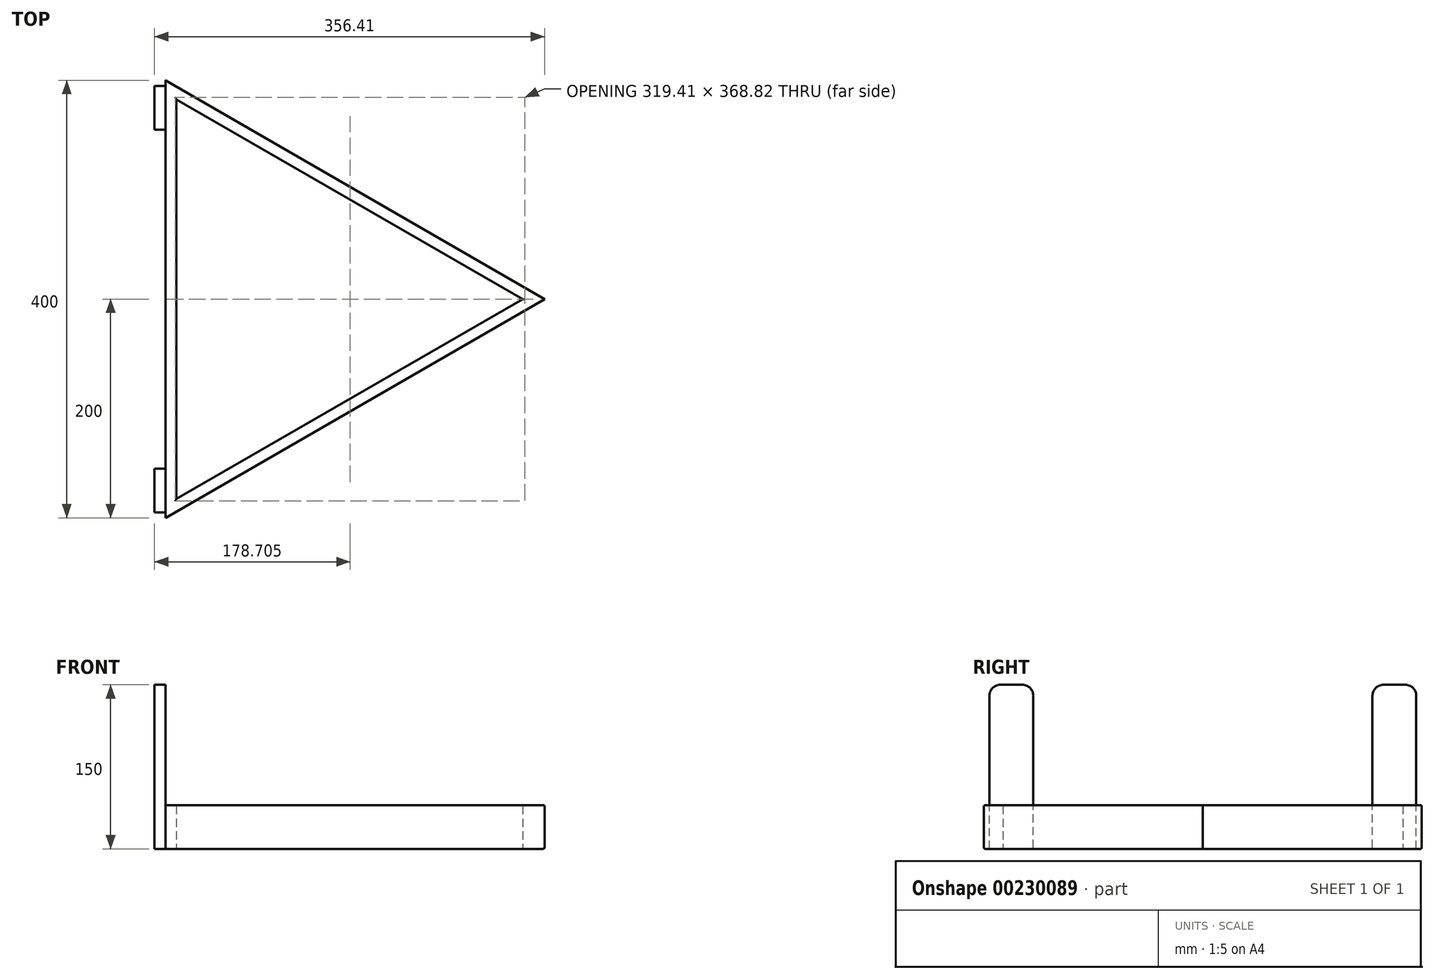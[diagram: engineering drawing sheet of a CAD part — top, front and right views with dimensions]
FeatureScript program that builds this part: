
annotation { "Feature Type Name" : "Feature", "Feature Type Description" : "" }
export const myFeature = defineFeature(function(context is Context, id is Id, definition is map)
    precondition{}
    {
        {
            var Q0;
            Q0=qCreatedBy(makeId("Top.planeOp"),FACE);
            var sketch = newSketch(context, id + "F0", { "sketchPlane" : qUnion([Q0])});
            skLineSegment(sketch, "E0", {"start": v(0, 0) * mm, "end": v(-346.41, 200) * mm});
            skLineSegment(sketch, "E1", {"start": v(-346.41, 200) * mm, "end": v(-346.41, -200) * mm});
            skLineSegment(sketch, "E2", {"start": v(-346.41, -200) * mm, "end": v(0, 0) * mm});
            skLineSegment(sketch, "E3", {"start": v(-20, 0) * mm, "end": v(-336.41, 182.68) * mm});
            skLineSegment(sketch, "E4", {"start": v(-336.41, 182.68) * mm, "end": v(-336.41, -182.68) * mm});
            skLineSegment(sketch, "E5", {"start": v(-336.41, -182.68) * mm, "end": v(-20, 0) * mm});
            skSolve(sketch);
        }
        {
            var Q0;
            Q0=qSketchRegion(id+"F0",true);
            extrude(context, id + "F1", {"entities" : qUnion([Q0]), "depth" : 40 * mm});
        }
        {
            var Q0;
            Q0=makeQuery(id+"F1.opExtrude","SWEPT_FACE",FACE,{"disambiguationData":[OSD([sQuery(id+"F0.wireOp",EDGE,"E1")])]});
            var sketch = newSketch(context, id + "F2", { "sketchPlane" : qUnion([Q0])});
            skLineSegment(sketch, "E6.bottom", {"start": v(-195, 0) * mm, "end": v(-155, 0) * mm});
            skLineSegment(sketch, "E6.top", {"start": v(-185, 150) * mm, "end": v(-165, 150) * mm});
            skLineSegment(sketch, "E6.left", {"start": v(-195, 0) * mm, "end": v(-195, 140) * mm});
            skLineSegment(sketch, "E6.right", {"start": v(-155, 0) * mm, "end": v(-155, 140) * mm});
            skLineSegment(sketch, "E7.bottom", {"start": v(195, 0) * mm, "end": v(155, 0) * mm});
            skLineSegment(sketch, "E7.top", {"start": v(185, 150) * mm, "end": v(165, 150) * mm});
            skLineSegment(sketch, "E7.left", {"start": v(195, 0) * mm, "end": v(195, 140) * mm});
            skLineSegment(sketch, "E7.right", {"start": v(155, 0) * mm, "end": v(155, 140) * mm});
            skPoint(sketch, "E8.visualSharp", {"position": v(-195, 150) * mm});
            skArc(sketch, "E8.filletArc", {"start": v(-185, 150) * mm, "mid": v(-192.07, 147.07) * mm, "end": v(-195, 140) * mm});
            skPoint(sketch, "E9.visualSharp", {"position": v(-155, 150) * mm});
            skArc(sketch, "E9.filletArc", {"start": v(-155, 140) * mm, "mid": v(-157.93, 147.07) * mm, "end": v(-165, 150) * mm});
            skPoint(sketch, "E10.visualSharp", {"position": v(155, 150) * mm});
            skArc(sketch, "E10.filletArc", {"start": v(165, 150) * mm, "mid": v(157.93, 147.07) * mm, "end": v(155, 140) * mm});
            skPoint(sketch, "E11.visualSharp", {"position": v(195, 150) * mm});
            skArc(sketch, "E11.filletArc", {"start": v(195, 140) * mm, "mid": v(192.07, 147.07) * mm, "end": v(185, 150) * mm});
            skSolve(sketch);
        }
        {
            var Q0;
            Q0=qSketchRegion(id+"F2",true);
            extrude(context, id + "F3", {"entities" : qUnion([Q0]), "operationType" : NewBodyOperationType.ADD, "depth" : 10 * mm});
        }
        {
            var Q0;
            {var subQ0=sQuery(id+"F2.wireOp",EDGE,"E6.right");var subQ1=sQuery(id+"F0.wireOp",EDGE,"E1");var subQ2=makeQuery(id+"F1.opExtrude","SWEPT_FACE",FACE,{"disambiguationData":[OSD([subQ1])]});var subQ3=makeQuery(id+"F1.opExtrude","CAP_FACE",FACE,{"disambiguationData":[OSD([sQuery(id+"F0.wireOp",EDGE,"E0"),subQ1,sQuery(id+"F0.wireOp",EDGE,"E2"),sQuery(id+"F0.wireOp",EDGE,"E3"),sQuery(id+"F0.wireOp",EDGE,"E4"),sQuery(id+"F0.wireOp",EDGE,"E5")])],"isStart":false});Q0=makeQuery(id+"F3.boolean.opBoolean","SPLIT",EDGE,{"disambiguationData":[topologyDisambiguationEdgeConnected([subQ3,subQ2]),TD([makeQuery(id+"F3.opExtrude","SWEPT_FACE",FACE,{"disambiguationData":[OSD([subQ0])]})])],"derivedFrom":makeQuery(id+"F1.opExtrude","CAP_EDGE",EDGE,{"disambiguationData":[OSD([subQ1])],"isStart":false})});}
            var Q1;
            Q1=makeQuery(id+"F1.opExtrude","CAP_EDGE",EDGE,{"disambiguationData":[OSD([sQuery(id+"F0.wireOp",EDGE,"E3")])],"isStart":false});
            var Q2;
            Q2=makeQuery(id+"F1.opExtrude","CAP_EDGE",EDGE,{"disambiguationData":[OSD([sQuery(id+"F0.wireOp",EDGE,"E0")])],"isStart":false});
            var Q3;
            Q3=makeQuery(id+"F1.opExtrude","CAP_EDGE",EDGE,{"disambiguationData":[OSD([sQuery(id+"F0.wireOp",EDGE,"E2")])],"isStart":false});
            var Q4;
            Q4=makeQuery(id+"F1.opExtrude","CAP_EDGE",EDGE,{"disambiguationData":[OSD([sQuery(id+"F0.wireOp",EDGE,"E5")])],"isStart":false});
            var Q5;
            Q5=makeQuery(id+"F1.opExtrude","CAP_EDGE",EDGE,{"disambiguationData":[OSD([sQuery(id+"F0.wireOp",EDGE,"E4")])],"isStart":false});
            var Q6;
            Q6=makeQuery(id+"F1.opExtrude","CAP_EDGE",EDGE,{"disambiguationData":[OSD([sQuery(id+"F0.wireOp",EDGE,"E2")])],"isStart":true});
            var Q7;
            Q7=makeQuery(id+"F1.opExtrude","CAP_EDGE",EDGE,{"disambiguationData":[OSD([sQuery(id+"F0.wireOp",EDGE,"E0")])],"isStart":true});
            var Q8;
            {var subQ0=sQuery(id+"F0.wireOp",EDGE,"E1");Q8=makeQuery(id+"F3.boolean.opBoolean","SPLIT",EDGE,{"disambiguationData":[TD([makeQuery(id+"F3.opExtrude","SWEPT_FACE",FACE,{"disambiguationData":[OSD([sQuery(id+"F2.wireOp",EDGE,"E6.right")])]})])],"derivedFrom":makeQuery(id+"F1.opExtrude","CAP_EDGE",EDGE,{"disambiguationData":[OSD([subQ0])],"isStart":true})});}
            var Q9;
            Q9=makeQuery(id+"F1.opExtrude","CAP_EDGE",EDGE,{"disambiguationData":[OSD([sQuery(id+"F0.wireOp",EDGE,"E5")])],"isStart":true});
            var Q10;
            Q10=makeQuery(id+"F1.opExtrude","CAP_EDGE",EDGE,{"disambiguationData":[OSD([sQuery(id+"F0.wireOp",EDGE,"E3")])],"isStart":true});
            var Q11;
            Q11=makeQuery(id+"F1.opExtrude","CAP_EDGE",EDGE,{"disambiguationData":[OSD([sQuery(id+"F0.wireOp",EDGE,"E4")])],"isStart":true});
            fillet(context, id + "F4", {"entities" : qUnion([Q0, Q1, Q2, Q3, Q4, Q5, Q6, Q7, Q8, Q9, Q10, Q11]), "radius" : 1 * mm, "tangentPropagation" : true, "allowEdgeOverflow" : false});
        }
    });
